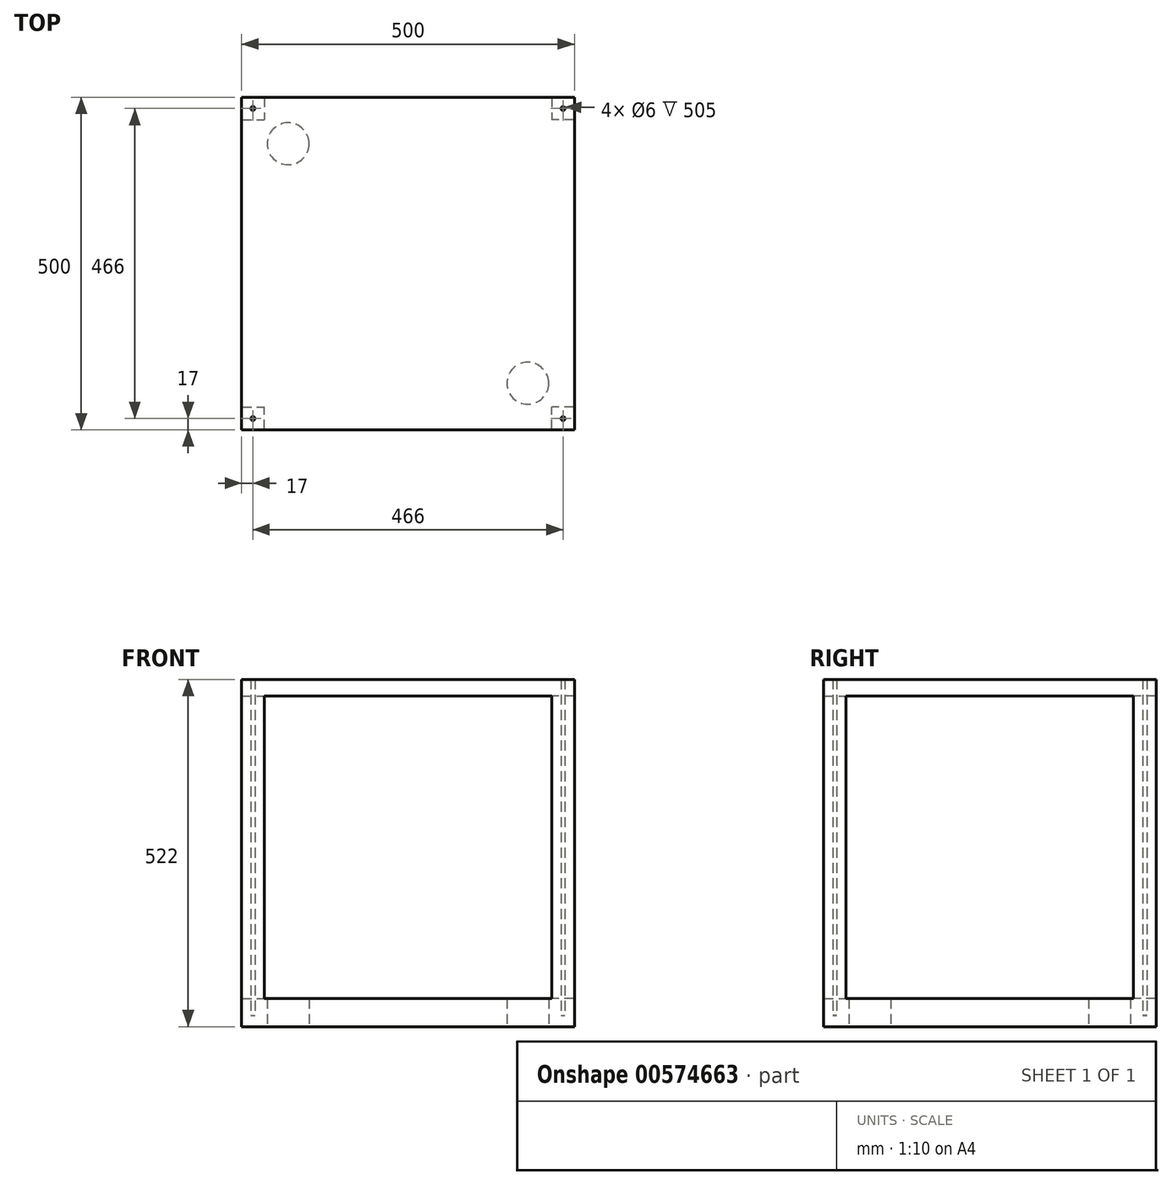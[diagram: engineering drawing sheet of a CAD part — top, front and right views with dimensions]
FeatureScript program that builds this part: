
annotation { "Feature Type Name" : "Feature", "Feature Type Description" : "" }
export const myFeature = defineFeature(function(context is Context, id is Id, definition is map)
    precondition{}
    {
        {
            var Q0;
            Q0=qCreatedBy(makeId("Top.planeOp"),FACE);
            var sketch = newSketch(context, id + "F0", { "sketchPlane" : qUnion([Q0])});
            skLineSegment(sketch, "E0.bottom", {"start": v(250, -250) * mm, "end": v(-250, -250) * mm});
            skLineSegment(sketch, "E0.top", {"start": v(250, 250) * mm, "end": v(-250, 250) * mm});
            skLineSegment(sketch, "E0.left", {"start": v(250, -250) * mm, "end": v(250, 250) * mm});
            skLineSegment(sketch, "E0.right", {"start": v(-250, -250) * mm, "end": v(-250, 250) * mm});
            skPoint(sketch, "E0.middle", {"position": v(0, 0) * mm});
            skPoint(sketch, "E1", {"position": v(-233, -233) * mm});
            skPoint(sketch, "E2.MirrorP", {"position": v(233, -233) * mm});
            skPoint(sketch, "E3.MirrorP", {"position": v(-233, 233) * mm});
            skPoint(sketch, "E4.MirrorP", {"position": v(233, 233) * mm});
            skPoint(sketch, "E5", {"position": v(-180, -180) * mm});
            skCircle(sketch, "E6", {"center": v(-180, -180) * mm, "radius": 31.5 * mm});
            skCircle(sketch, "E7.MirrorC", {"center": v(180, -180) * mm, "radius": 31.5 * mm});
            skCircle(sketch, "E8.MirrorC", {"center": v(-180, 180) * mm, "radius": 31.5 * mm});
            skPoint(sketch, "E9.MirrorP", {"position": v(180, 180) * mm});
            skCircle(sketch, "E10.MirrorC", {"center": v(180, 180) * mm, "radius": 31.5 * mm});
            skSolve(sketch);
        }
        {
            var Q0;
            Q0=makeQuery(id+"F0.imprint","IMPRINT",FACE,{"disambiguationData":[TD([[makeQuery(id+"F0.imprint","IMPRINT",EDGE,{"derivedFrom":sQuery(id+"F0.wireOp",EDGE,"E0.bottom")}),-1.0]])]});
            var Q1;
            Q1=makeQuery(id+"F0.imprint","IMPRINT",FACE,{"disambiguationData":[TD([[makeQuery(id+"F0.imprint","IMPRINT",EDGE,{"derivedFrom":sQuery(id+"F0.wireOp",EDGE,"E6")}),1.0]])]});
            var Q2;
            Q2=makeQuery(id+"F0.imprint","IMPRINT",FACE,{"disambiguationData":[TD([[makeQuery(id+"F0.imprint","IMPRINT",EDGE,{"derivedFrom":sQuery(id+"F0.wireOp",EDGE,"E7.MirrorC")}),-1.0]])]});
            var Q3;
            Q3=makeQuery(id+"F0.imprint","IMPRINT",FACE,{"disambiguationData":[TD([[makeQuery(id+"F0.imprint","IMPRINT",EDGE,{"derivedFrom":sQuery(id+"F0.wireOp",EDGE,"E8.MirrorC")}),-1.0]])]});
            var Q4;
            Q4=makeQuery(id+"F0.imprint","IMPRINT",FACE,{"disambiguationData":[TD([[makeQuery(id+"F0.imprint","IMPRINT",EDGE,{"derivedFrom":sQuery(id+"F0.wireOp",EDGE,"E10.MirrorC")}),1.0]])]});
            extrude(context, id + "F1", {"entities" : qUnion([Q0, Q1, Q2, Q3, Q4]), "depth" : 25 * mm, "offsetDistance" : 25 * mm});
        }
        {
            var Q0;
            Q0=makeQuery(id+"F1.opExtrude","CAP_FACE",FACE,{"disambiguationData":[OSD([sQuery(id+"F0.wireOp",EDGE,"E0.bottom"),sQuery(id+"F0.wireOp",EDGE,"E0.top"),sQuery(id+"F0.wireOp",EDGE,"E0.left"),sQuery(id+"F0.wireOp",EDGE,"E0.right")])],"isStart":false});
            var sketch = newSketch(context, id + "F2", { "sketchPlane" : qUnion([Q0])});
            skLineSegment(sketch, "E11.bottom", {"start": v(-250, 250) * mm, "end": v(-216, 250) * mm});
            skLineSegment(sketch, "E11.top", {"start": v(-250, 216) * mm, "end": v(-216, 216) * mm});
            skLineSegment(sketch, "E11.left", {"start": v(-250, 250) * mm, "end": v(-250, 216) * mm});
            skLineSegment(sketch, "E11.right", {"start": v(-216, 250) * mm, "end": v(-216, 216) * mm});
            skLineSegment(sketch, "E12.MirrorCS", {"start": v(216, 250) * mm, "end": v(216, 216) * mm});
            skLineSegment(sketch, "E13.MirrorCS", {"start": v(250, 216) * mm, "end": v(216, 216) * mm});
            skLineSegment(sketch, "E14.MirrorCS", {"start": v(250, 250) * mm, "end": v(216, 250) * mm});
            skLineSegment(sketch, "E15.MirrorCS", {"start": v(250, 250) * mm, "end": v(250, 216) * mm});
            skLineSegment(sketch, "E16.MirrorCS", {"start": v(-250, -216) * mm, "end": v(-216, -216) * mm});
            skLineSegment(sketch, "E17.MirrorCS", {"start": v(-216, -250) * mm, "end": v(-216, -216) * mm});
            skLineSegment(sketch, "E18.MirrorCS", {"start": v(-250, -250) * mm, "end": v(-216, -250) * mm});
            skLineSegment(sketch, "E19.MirrorCS", {"start": v(-250, -250) * mm, "end": v(-250, -216) * mm});
            skLineSegment(sketch, "E20.MirrorCS", {"start": v(216, -250) * mm, "end": v(216, -216) * mm});
            skLineSegment(sketch, "E21.MirrorCS", {"start": v(250, -250) * mm, "end": v(216, -250) * mm});
            skLineSegment(sketch, "E22.MirrorCS", {"start": v(250, -216) * mm, "end": v(216, -216) * mm});
            skLineSegment(sketch, "E23.MirrorCS", {"start": v(250, -250) * mm, "end": v(250, -216) * mm});
            skSolve(sketch);
        }
        {
            var Q0;
            Q0=makeQuery(id+"F2.imprint","IMPRINT",FACE,{"disambiguationData":[TD([[makeQuery(id+"F2.imprint","IMPRINT",EDGE,{"derivedFrom":sQuery(id+"F2.wireOp",EDGE,"E11.bottom")}),1.0]])]});
            var Q1;
            Q1=makeQuery(id+"F2.imprint","IMPRINT",FACE,{"disambiguationData":[TD([[makeQuery(id+"F2.imprint","IMPRINT",EDGE,{"derivedFrom":sQuery(id+"F2.wireOp",EDGE,"E12.MirrorCS")}),1.0]])]});
            var Q2;
            Q2=makeQuery(id+"F2.imprint","IMPRINT",FACE,{"disambiguationData":[TD([[makeQuery(id+"F2.imprint","IMPRINT",EDGE,{"derivedFrom":sQuery(id+"F2.wireOp",EDGE,"E20.MirrorCS")}),-1.0]])]});
            var Q3;
            Q3=makeQuery(id+"F2.imprint","IMPRINT",FACE,{"disambiguationData":[TD([[makeQuery(id+"F2.imprint","IMPRINT",EDGE,{"derivedFrom":sQuery(id+"F2.wireOp",EDGE,"E16.MirrorCS")}),-1.0]])]});
            extrude(context, id + "F3", {"entities" : qUnion([Q0, Q1, Q2, Q3]), "operationType" : NewBodyOperationType.ADD, "depth" : 455 * mm, "offsetDistance" : 25 * mm});
        }
        {
            var Q0;
            Q0=makeQuery(id+"F3.opExtrude","CAP_FACE",FACE,{"disambiguationData":[OSD([sQuery(id+"F2.wireOp",EDGE,"E11.bottom"),sQuery(id+"F2.wireOp",EDGE,"E11.top"),sQuery(id+"F2.wireOp",EDGE,"E11.left"),sQuery(id+"F2.wireOp",EDGE,"E11.right")])],"isStart":false});
            var sketch = newSketch(context, id + "F4", { "sketchPlane" : qUnion([Q0])});
            skPoint(sketch, "E24.0", {"position": v(250, -250) * mm});
            skLineSegment(sketch, "E25.bottom", {"start": v(250, -250) * mm, "end": v(-250, -250) * mm});
            skLineSegment(sketch, "E25.top", {"start": v(250, 250) * mm, "end": v(-250, 250) * mm});
            skLineSegment(sketch, "E25.left", {"start": v(250, -250) * mm, "end": v(250, 250) * mm});
            skLineSegment(sketch, "E25.right", {"start": v(-250, -250) * mm, "end": v(-250, 250) * mm});
            skSolve(sketch);
        }
        {
            var Q0;
            {var subQ2=sQuery(id+"F4.wireOp",EDGE,"E25.bottom");Q0=makeQuery(id+"F4.imprint","IMPRINT",FACE,{"disambiguationData":[TD([[makeQuery(id+"F4.imprint","IMPRINT",EDGE,{"derivedFrom":subQ2}),-1.0]])]});}
            var Q1;
            {var subQ4=makeQuery(id+"F3.opExtrude","CAP_EDGE",EDGE,{"disambiguationData":[OSD([sQuery(id+"F2.wireOp",EDGE,"E11.top")])],"isStart":false});Q1=makeQuery(id+"F4.imprint","IMPRINT",FACE,{"disambiguationData":[TD([[makeQuery(id+"F4.imprint","IMPRINT",EDGE,{"derivedFrom":subQ4}),1.0]])]});}
            extrude(context, id + "F5", {"entities" : qUnion([Q0, Q1]), "operationType" : NewBodyOperationType.ADD, "depth" : 25 * mm, "offsetDistance" : 25 * mm});
        }
        {
            var Q0;
            Q0=makeQuery(id+"F0.imprint","IMPRINT",FACE,{"disambiguationData":[TD([[makeQuery(id+"F0.imprint","IMPRINT",EDGE,{"derivedFrom":sQuery(id+"F0.wireOp",EDGE,"E6")}),1.0]])]});
            var Q1;
            Q1=makeQuery(id+"F0.imprint","IMPRINT",FACE,{"disambiguationData":[TD([[makeQuery(id+"F0.imprint","IMPRINT",EDGE,{"derivedFrom":sQuery(id+"F0.wireOp",EDGE,"E8.MirrorC")}),-1.0]])]});
            var Q2;
            Q2=makeQuery(id+"F0.imprint","IMPRINT",FACE,{"disambiguationData":[TD([[makeQuery(id+"F0.imprint","IMPRINT",EDGE,{"derivedFrom":sQuery(id+"F0.wireOp",EDGE,"E10.MirrorC")}),1.0]])]});
            var Q3;
            Q3=makeQuery(id+"F0.imprint","IMPRINT",FACE,{"disambiguationData":[TD([[makeQuery(id+"F0.imprint","IMPRINT",EDGE,{"derivedFrom":sQuery(id+"F0.wireOp",EDGE,"E7.MirrorC")}),-1.0]])]});
            extrude(context, id + "F6", {"entities" : qUnion([Q0, Q1, Q2, Q3]), "operationType" : NewBodyOperationType.ADD, "oppositeDirection" : true, "depth" : 17 * mm, "offsetDistance" : 25 * mm});
        }
        {
            var Q0;
            Q0=sQuery(id+"F0.wireOp",VERTEX,"E1");
            var Q1;
            Q1=sQuery(id+"F0.wireOp",VERTEX,"E2.MirrorP");
            var Q2;
            Q2=sQuery(id+"F0.wireOp",VERTEX,"E4.MirrorP");
            var Q3;
            Q3=sQuery(id+"F0.wireOp",VERTEX,"E3.MirrorP");
            var Q4;
            Q4=makeQuery(id+"F1.opExtrude","SWEPT_BODY",BODY,{"disambiguationData":[OSD([sQuery(id+"F0.wireOp",EDGE,"E0.bottom"),sQuery(id+"F0.wireOp",EDGE,"E0.top"),sQuery(id+"F0.wireOp",EDGE,"E0.left"),sQuery(id+"F0.wireOp",EDGE,"E0.right")])]});
            hole(context, id + "F7", {"style" : HoleStyle.SIMPLE, "endStyle" : HoleEndStyle.THROUGH, "oppositeDirection" : true, "holeDiameter" : 6 * mm, "isTappedThrough" : true, "tappedDepth" : 6 * mm, "tapClearance" : 3, "locations" : qUnion([Q0, Q1, Q2, Q3]), "scope" : qUnion([Q4])});
        }
    });
